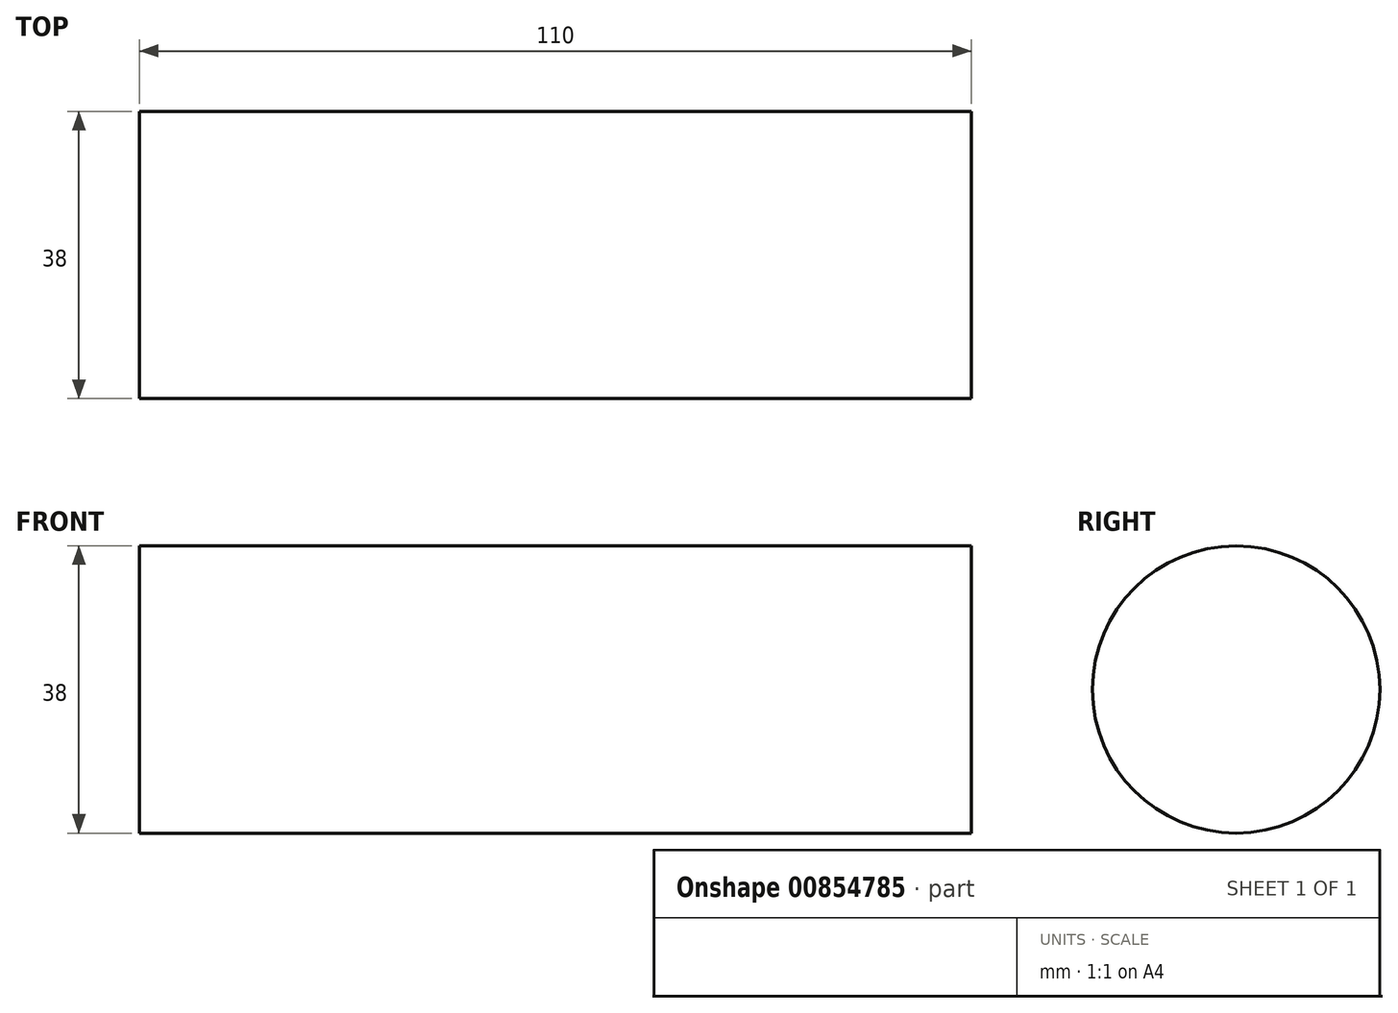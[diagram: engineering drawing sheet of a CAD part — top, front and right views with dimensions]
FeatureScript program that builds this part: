
annotation { "Feature Type Name" : "Feature", "Feature Type Description" : "" }
export const myFeature = defineFeature(function(context is Context, id is Id, definition is map)
    precondition{}
    {
        {
            var Q0;
            Q0=qCreatedBy(makeId("Right.planeOp"),FACE);
            var sketch = newSketch(context, id + "F0", { "sketchPlane" : qUnion([Q0])});
            skCircle(sketch, "E0", {"center": v(0, 0) * mm, "radius": 19 * mm});
            skSolve(sketch);
        }
        {
            var Q0;
            Q0 = qSketchRegion(id + "F0", true);
            extrude(context, id + "F1", {"entities" : qUnion([Q0]), "depth" : 110 * mm, "offsetDistance" : 25 * mm});
        }
    });
